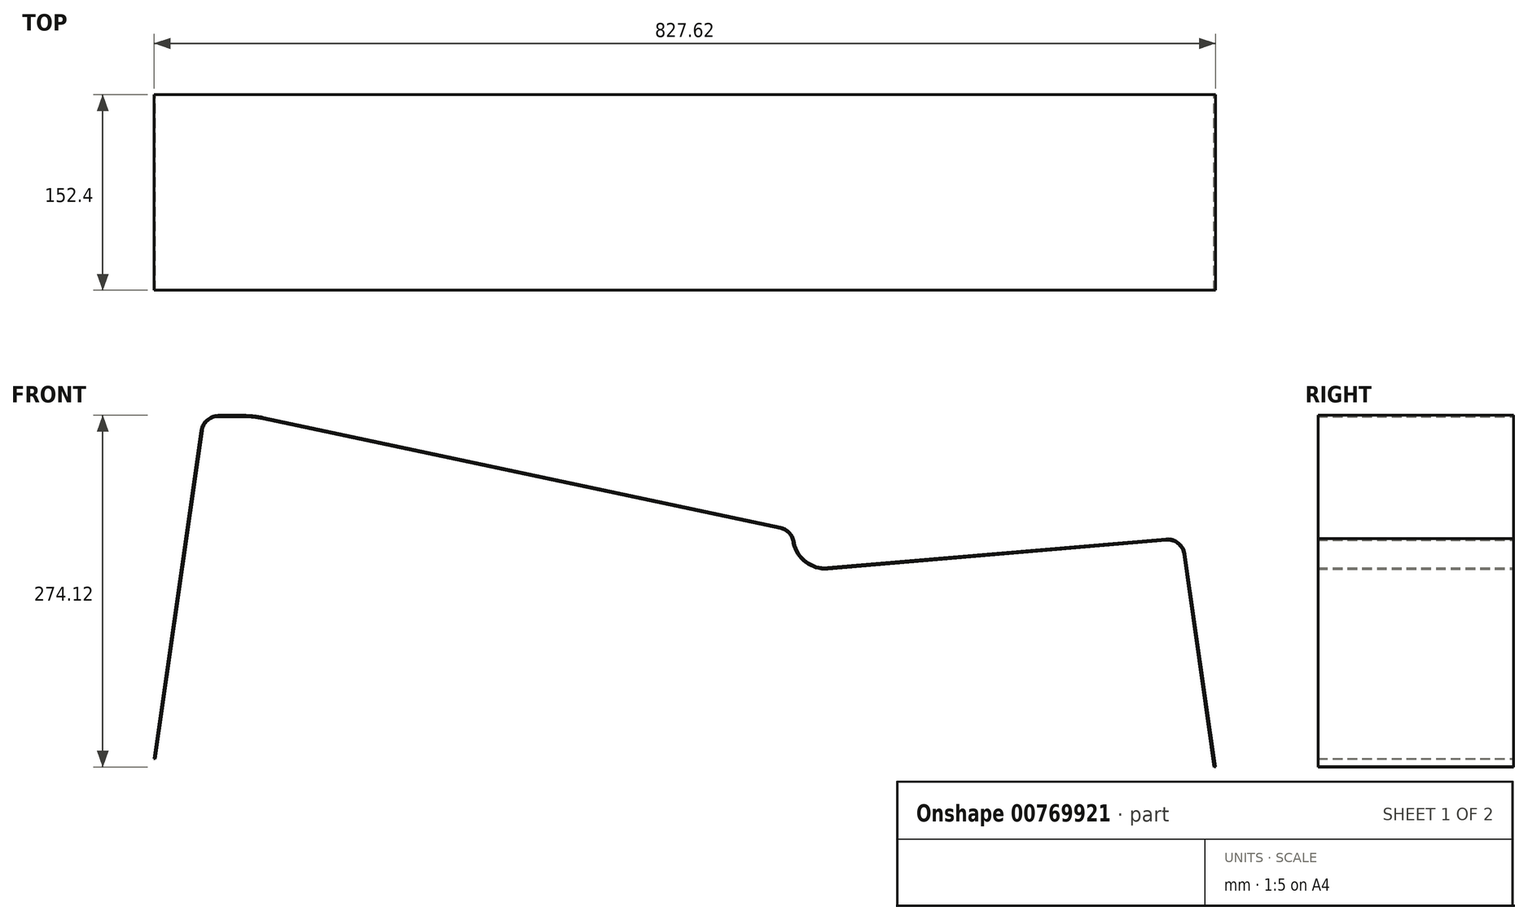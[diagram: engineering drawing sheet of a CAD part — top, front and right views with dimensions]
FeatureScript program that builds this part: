
annotation { "Feature Type Name" : "Feature", "Feature Type Description" : "" }
export const myFeature = defineFeature(function(context is Context, id is Id, definition is map)
    precondition{}
    {
        {
            var Q0;
            Q0=qCreatedBy(makeId("Front.planeOp"),FACE);
            var sketch = newSketch(context, id + "F0", { "sketchPlane" : qUnion([Q0])});
            skLineSegment(sketch, "E0", {"start": v(0, 0) * mm, "end": v(36.54, 255.8) * mm});
            skLineSegment(sketch, "E1", {"start": v(49.11, 266.7) * mm, "end": v(68.2, 266.7) * mm});
            skLineSegment(sketch, "E2", {"start": v(84.02, 265.04) * mm, "end": v(487.12, 179.53) * mm});
            skLineSegment(sketch, "E3", {"start": v(496.94, 169.6) * mm, "end": v(497.2, 168.3) * mm});
            skLineSegment(sketch, "E4", {"start": v(524.26, 147.97) * mm, "end": v(788.15, 170.43) * mm});
            skLineSegment(sketch, "E5", {"start": v(801.8, 159.57) * mm, "end": v(825.5, -6.35) * mm});
            skLineSegment(sketch, "E6", {"start": v(312.49, 146.05) * mm, "end": v(1020.8, 146.05) * mm, "construction": true});
            skPoint(sketch, "E7.visualSharp", {"position": v(38.1, 266.7) * mm});
            skArc(sketch, "E7.filletArc", {"start": v(49.11, 266.7) * mm, "mid": v(40.8, 263.6) * mm, "end": v(36.54, 255.8) * mm});
            skPoint(sketch, "E8.visualSharp", {"position": v(76.2, 266.7) * mm});
            skArc(sketch, "E8.filletArc", {"start": v(84.02, 265.04) * mm, "mid": v(76.16, 266.28) * mm, "end": v(68.2, 266.7) * mm});
            skPoint(sketch, "E9.visualSharp", {"position": v(495.3, 177.8) * mm});
            skArc(sketch, "E9.filletArc", {"start": v(496.94, 169.6) * mm, "mid": v(493.52, 176.04) * mm, "end": v(487.12, 179.53) * mm});
            skPoint(sketch, "E10.visualSharp", {"position": v(501.65, 146.05) * mm});
            skArc(sketch, "E10.filletArc", {"start": v(497.2, 168.3) * mm, "mid": v(506.85, 152.97) * mm, "end": v(524.26, 147.97) * mm});
            skPoint(sketch, "E11.visualSharp", {"position": v(800.1, 171.45) * mm});
            skArc(sketch, "E11.filletArc", {"start": v(801.8, 159.57) * mm, "mid": v(797.13, 167.72) * mm, "end": v(788.15, 170.43) * mm});
            skLineSegment(sketch, "E12.0", {"start": v(802.85, 159.73) * mm, "end": v(826.56, -6.2) * mm});
            skArc(sketch, "E12.1", {"start": v(84.24, 266.09) * mm, "mid": v(76.27, 267.35) * mm, "end": v(68.2, 267.77) * mm});
            skLineSegment(sketch, "E12.2", {"start": v(49.11, 267.77) * mm, "end": v(68.2, 267.77) * mm});
            skArc(sketch, "E12.3", {"start": v(49.11, 267.77) * mm, "mid": v(40.1, 264.4) * mm, "end": v(35.49, 255.95) * mm});
            skLineSegment(sketch, "E12.4", {"start": v(-1.06, 0.15) * mm, "end": v(35.49, 255.95) * mm});
            skLineSegment(sketch, "E12.5", {"start": v(84.24, 266.09) * mm, "end": v(487.34, 180.58) * mm});
            skArc(sketch, "E12.6", {"start": v(497.99, 169.81) * mm, "mid": v(494.28, 176.79) * mm, "end": v(487.34, 180.58) * mm});
            skLineSegment(sketch, "E12.7", {"start": v(497.99, 169.81) * mm, "end": v(498.25, 168.51) * mm});
            skArc(sketch, "E12.8", {"start": v(498.25, 168.51) * mm, "mid": v(507.5, 153.83) * mm, "end": v(524.17, 149.04) * mm});
            skLineSegment(sketch, "E12.9", {"start": v(524.17, 149.04) * mm, "end": v(788.06, 171.5) * mm});
            skArc(sketch, "E12.10", {"start": v(802.85, 159.73) * mm, "mid": v(797.8, 168.55) * mm, "end": v(788.06, 171.5) * mm});
            skLineSegment(sketch, "E13", {"start": v(0, 0) * mm, "end": v(-1.06, 0.15) * mm});
            skLineSegment(sketch, "E14", {"start": v(826.56, -6.2) * mm, "end": v(825.5, -6.35) * mm});
            skSolve(sketch);
        }
        {
            var Q0;
            Q0 = qSketchRegion(id + "F0", true);
            extrude(context, id + "F1", {"entities" : qUnion([Q0]), "depth" : 152.4 * mm, "offsetDistance" : 25.4 * mm});
        }
    });
